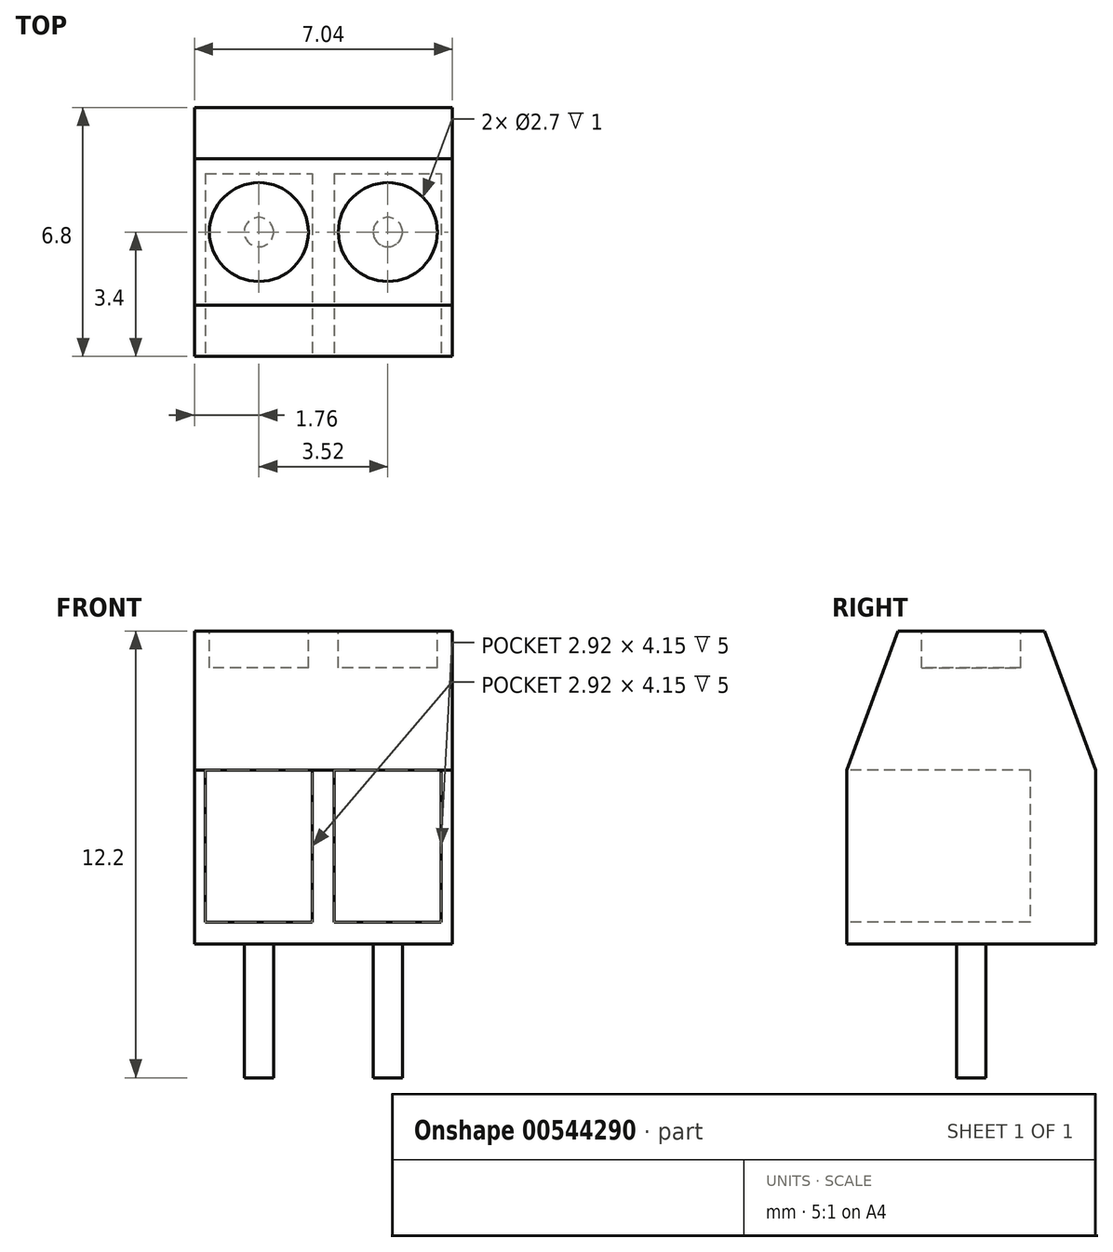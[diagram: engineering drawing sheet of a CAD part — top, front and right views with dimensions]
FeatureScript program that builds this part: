
annotation { "Feature Type Name" : "Feature", "Feature Type Description" : "" }
export const myFeature = defineFeature(function(context is Context, id is Id, definition is map)
    precondition{}
    {
        {
            var Q0;
            Q0=qCreatedBy(makeId("Front.planeOp"),FACE);
            var sketch = newSketch(context, id + "F0", { "sketchPlane" : qUnion([Q0])});
            skLineSegment(sketch, "E0.bottom", {"start": v(0, 0) * mm, "end": v(7.04, 0) * mm});
            skLineSegment(sketch, "E0.top", {"start": v(0, 8.55) * mm, "end": v(7.04, 8.55) * mm});
            skLineSegment(sketch, "E0.left", {"start": v(0, 0) * mm, "end": v(0, 8.55) * mm});
            skLineSegment(sketch, "E0.right", {"start": v(7.04, 0) * mm, "end": v(7.04, 8.55) * mm});
            skSolve(sketch);
        }
        {
            var Q0;
            Q0=qSketchRegion(id+"F0",true);
            extrude(context, id + "F1", {"entities" : qUnion([Q0]), "depth" : 6.8 * mm});
        }
        {
            var Q0;
            Q0=makeQuery(id+"F1.opExtrude","SWEPT_FACE",FACE,{"disambiguationData":[OSD([sQuery(id+"F0.wireOp",EDGE,"E0.right")])]});
            var sketch = newSketch(context, id + "F2", { "sketchPlane" : qUnion([Q0])});
            skLineSegment(sketch, "E1", {"start": v(-3.4, 8.55) * mm, "end": v(-3.4, 0) * mm, "construction": true});
            skLineSegment(sketch, "E2", {"start": v(-6.8, 4.75) * mm, "end": v(-5.4, 8.55) * mm});
            skLineSegment(sketch, "E3", {"start": v(-5.4, 8.55) * mm, "end": v(-6.8, 8.55) * mm});
            skLineSegment(sketch, "E4", {"start": v(-6.8, 8.55) * mm, "end": v(-6.8, 4.75) * mm});
            skLineSegment(sketch, "E5.MirrorCS", {"start": v(0, 8.55) * mm, "end": v(0, 4.75) * mm});
            skLineSegment(sketch, "E6.MirrorCS", {"start": v(-1.4, 8.55) * mm, "end": v(0, 8.55) * mm});
            skLineSegment(sketch, "E7.MirrorCS", {"start": v(0, 4.75) * mm, "end": v(-1.4, 8.55) * mm});
            skSolve(sketch);
        }
        {
            var Q0;
            Q0=qSketchRegion(id+"F2",true);
            extrude(context, id + "F3", {"entities" : qUnion([Q0]), "operationType" : NewBodyOperationType.REMOVE, "endBound" : BoundingType.UP_TO_NEXT, "oppositeDirection" : true, "depth" : 25 * mm});
        }
        {
            var Q0;
            Q0=makeQuery(id+"F1.opExtrude","CAP_FACE",FACE,{"disambiguationData":[OSD([sQuery(id+"F0.wireOp",EDGE,"E0.bottom"),sQuery(id+"F0.wireOp",EDGE,"E0.top"),sQuery(id+"F0.wireOp",EDGE,"E0.left"),sQuery(id+"F0.wireOp",EDGE,"E0.right")])],"isStart":false});
            var sketch = newSketch(context, id + "F4", { "sketchPlane" : qUnion([Q0])});
            skLineSegment(sketch, "E8", {"start": v(3.52, 4.75) * mm, "end": v(3.52, 0) * mm, "construction": true});
            skLineSegment(sketch, "E9.bottom", {"start": v(0.3, 4.75) * mm, "end": v(3.22, 4.75) * mm});
            skLineSegment(sketch, "E9.top", {"start": v(0.3, 0.6) * mm, "end": v(3.22, 0.6) * mm});
            skLineSegment(sketch, "E9.left", {"start": v(0.3, 4.75) * mm, "end": v(0.3, 0.6) * mm});
            skLineSegment(sketch, "E9.right", {"start": v(3.22, 4.75) * mm, "end": v(3.22, 0.6) * mm});
            skLineSegment(sketch, "E10.MirrorCS", {"start": v(3.82, 4.75) * mm, "end": v(3.82, 0.6) * mm});
            skLineSegment(sketch, "E11.MirrorCS", {"start": v(6.74, 4.75) * mm, "end": v(6.74, 0.6) * mm});
            skLineSegment(sketch, "E12.MirrorCS", {"start": v(6.74, 0.6) * mm, "end": v(3.82, 0.6) * mm});
            skLineSegment(sketch, "E13.MirrorCS", {"start": v(6.74, 4.75) * mm, "end": v(3.82, 4.75) * mm});
            skSolve(sketch);
        }
        {
            var Q0;
            Q0=qSketchRegion(id+"F4",true);
            extrude(context, id + "F5", {"entities" : qUnion([Q0]), "operationType" : NewBodyOperationType.REMOVE, "oppositeDirection" : true, "depth" : 5 * mm});
        }
        {
            var Q0;
            Q0=makeQuery(id+"F1.opExtrude","SWEPT_FACE",FACE,{"disambiguationData":[OSD([sQuery(id+"F0.wireOp",EDGE,"E0.top")])]});
            var sketch = newSketch(context, id + "F6", { "sketchPlane" : qUnion([Q0])});
            skLineSegment(sketch, "E14", {"start": v(5.28, -1.4) * mm, "end": v(5.28, -5.4) * mm, "construction": true});
            skLineSegment(sketch, "E15", {"start": v(1.76, -1.4) * mm, "end": v(1.76, -5.4) * mm, "construction": true});
            skCircle(sketch, "E16", {"center": v(1.76, -3.4) * mm, "radius": 1.35 * mm});
            skCircle(sketch, "E17", {"center": v(5.28, -3.4) * mm, "radius": 1.35 * mm});
            skSolve(sketch);
        }
        {
            var Q0;
            Q0=qSketchRegion(id+"F6",true);
            extrude(context, id + "F7", {"entities" : qUnion([Q0]), "operationType" : NewBodyOperationType.REMOVE, "oppositeDirection" : true, "depth" : 1 * mm});
        }
        {
            var Q0;
            Q0=makeQuery(id+"F1.opExtrude","SWEPT_FACE",FACE,{"disambiguationData":[OSD([sQuery(id+"F0.wireOp",EDGE,"E0.bottom")])]});
            var sketch = newSketch(context, id + "F8", { "sketchPlane" : qUnion([Q0])});
            skLineSegment(sketch, "E18", {"start": v(1.76, 6.8) * mm, "end": v(1.76, 0) * mm, "construction": true});
            skLineSegment(sketch, "E19", {"start": v(5.28, 6.8) * mm, "end": v(5.28, 0) * mm, "construction": true});
            skCircle(sketch, "E20", {"center": v(1.76, 3.4) * mm, "radius": 0.4 * mm});
            skCircle(sketch, "E21", {"center": v(5.28, 3.4) * mm, "radius": 0.4 * mm});
            skSolve(sketch);
        }
        {
            var Q0;
            Q0=qSketchRegion(id+"F8",true);
            extrude(context, id + "F9", {"entities" : qUnion([Q0]), "operationType" : NewBodyOperationType.ADD, "depth" : 3.65 * mm});
        }
    });
